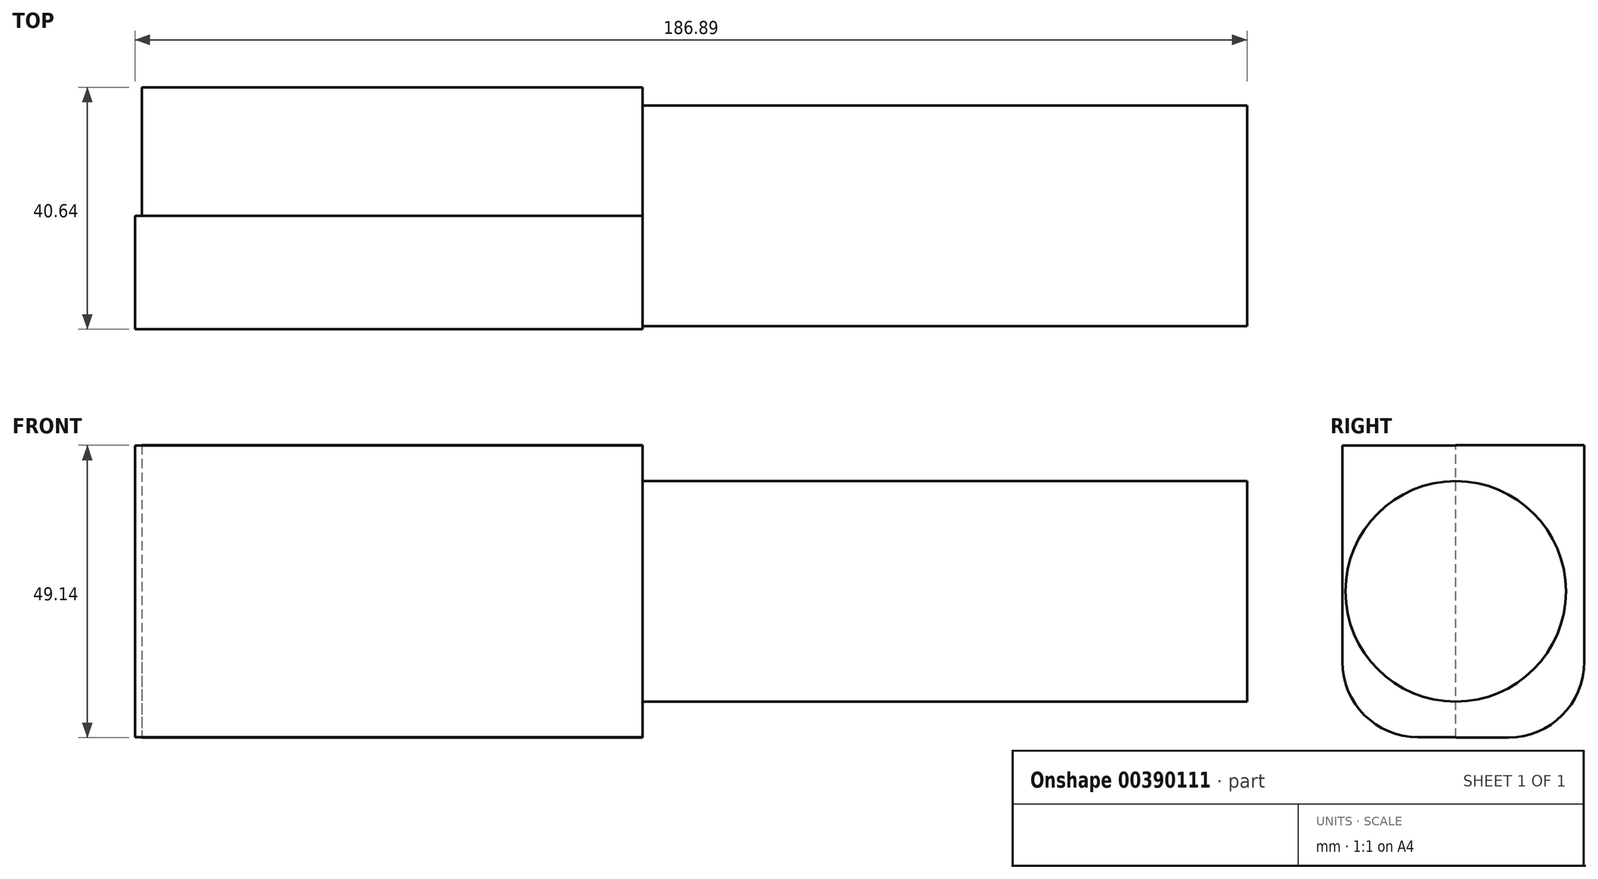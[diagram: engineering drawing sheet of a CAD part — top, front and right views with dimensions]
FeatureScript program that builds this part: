
annotation { "Feature Type Name" : "Feature", "Feature Type Description" : "" }
export const myFeature = defineFeature(function(context is Context, id is Id, definition is map)
    precondition{}
    {
        {
            var Q0;
            Q0=qCreatedBy(makeId("Right.planeOp"),FACE);
            var sketch = newSketch(context, id + "F0", { "sketchPlane" : qUnion([Q0])});
            skCircle(sketch, "E0", {"center": v(0, 0) * mm, "radius": 18.52 * mm});
            skSolve(sketch);
        }
        {
            var Q0;
            Q0 = qSketchRegion(id + "F0", true);
            extrude(context, id + "F1", {"entities" : qUnion([Q0]), "depth" : 101.6 * mm});
        }
        {
            var Q0;
            Q0=qCreatedBy(makeId("Front.planeOp"),FACE);
            var sketch = newSketch(context, id + "F2", { "sketchPlane" : qUnion([Q0])});
            skLineSegment(sketch, "E1.bottom", {"start": v(0, 24.57) * mm, "end": v(-84.1, 24.57) * mm});
            skLineSegment(sketch, "E1.top", {"start": v(0, -24.57) * mm, "end": v(-84.1, -24.57) * mm});
            skLineSegment(sketch, "E1.left", {"start": v(0, 24.57) * mm, "end": v(0, -24.57) * mm});
            skLineSegment(sketch, "E1.right", {"start": v(-84.1, 24.57) * mm, "end": v(-84.1, -24.57) * mm});
            skPoint(sketch, "E1.middle", {"position": v(-42.05, 0) * mm});
            skSolve(sketch);
        }
        {
            var Q0;
            Q0=qCreatedBy(makeId("Front.planeOp"),FACE);
            var sketch = newSketch(context, id + "F3", { "sketchPlane" : qUnion([Q0])});
            skLineSegment(sketch, "E2.bottom", {"start": v(0, -24.52) * mm, "end": v(-85.3, -24.52) * mm});
            skLineSegment(sketch, "E2.top", {"start": v(0, 24.52) * mm, "end": v(-85.3, 24.52) * mm});
            skLineSegment(sketch, "E2.left", {"start": v(0, -24.52) * mm, "end": v(0, 24.52) * mm});
            skLineSegment(sketch, "E2.right", {"start": v(-85.3, -24.52) * mm, "end": v(-85.3, 24.52) * mm});
            skPoint(sketch, "E2.middle", {"position": v(-42.65, 0) * mm});
            skSolve(sketch);
        }
        {
            var Q0;
            Q0 = qSketchRegion(id + "F3", true);
            extrude(context, id + "F4", {"entities" : qUnion([Q0]), "operationType" : NewBodyOperationType.ADD, "depth" : 19.05 * mm});
        }
        {
            var Q0;
            Q0=makeQuery(id+"F2.imprint","IMPRINT",FACE,{"disambiguationData":[TD([[makeQuery(id+"F2.imprint","IMPRINT",EDGE,{"derivedFrom":sQuery(id+"F2.wireOp",EDGE,"E1.bottom")}),1.0]])]});
            extrude(context, id + "F5", {"entities" : qUnion([Q0]), "operationType" : NewBodyOperationType.ADD, "oppositeDirection" : true, "depth" : 21.59 * mm});
        }
        {
            var Q0;
            Q0=makeQuery(id+"F5.opExtrude","CAP_EDGE",EDGE,{"disambiguationData":[OSD([sQuery(id+"F2.wireOp",EDGE,"E1.top")])],"isStart":false});
            var Q1;
            Q1=makeQuery(id+"F4.opExtrude","CAP_EDGE",EDGE,{"disambiguationData":[OSD([sQuery(id+"F3.wireOp",EDGE,"E2.bottom")])],"isStart":false});
            fillet(context, id + "F6", {"entities" : qUnion([Q0, Q1]), "radius" : 12.7 * mm, "tangentPropagation" : true, "allowEdgeOverflow" : false});
        }
    });
